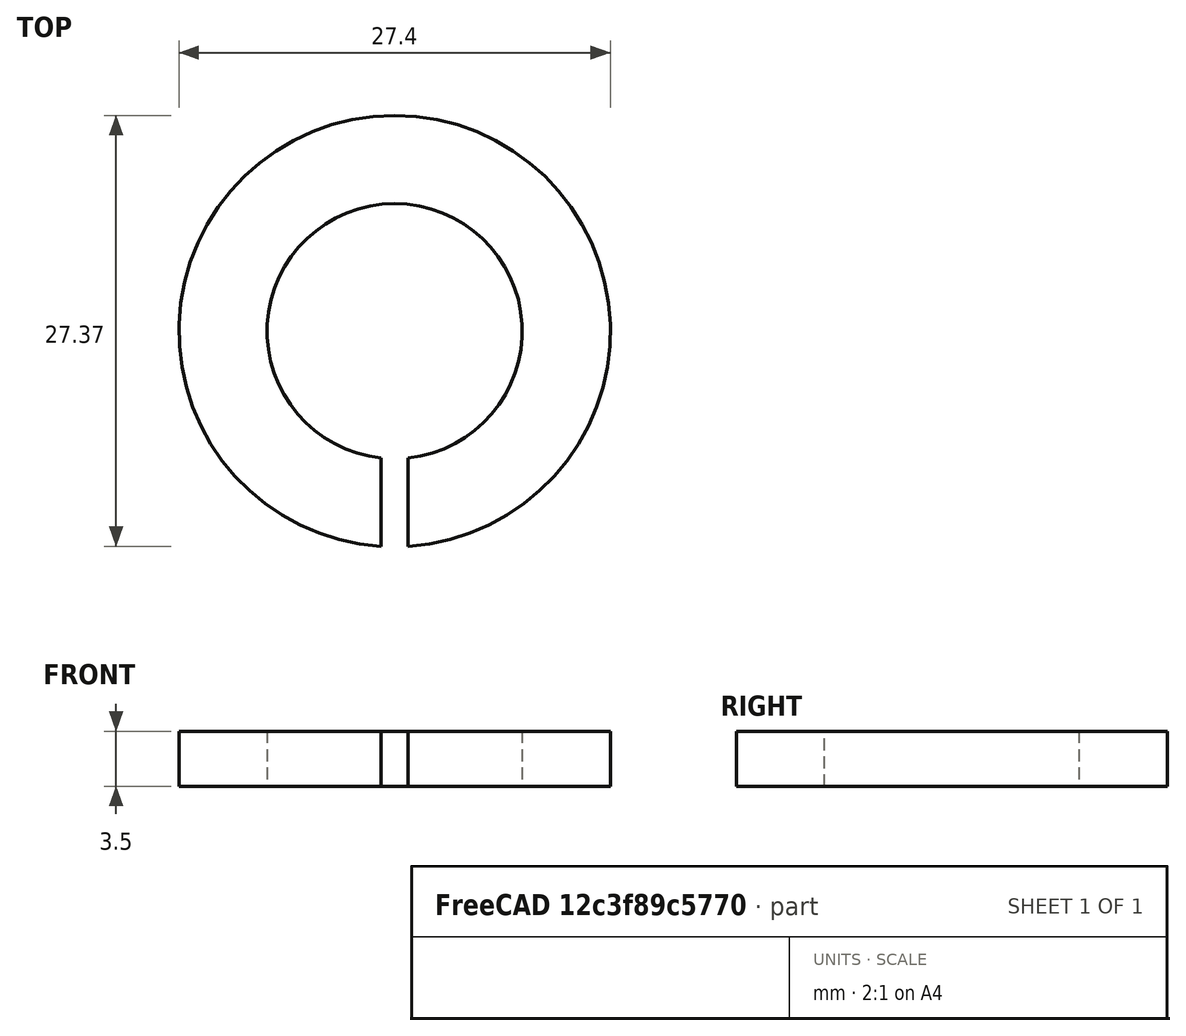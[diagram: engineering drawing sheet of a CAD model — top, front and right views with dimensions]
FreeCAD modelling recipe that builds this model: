
FCSTD DOCUMENT  (FreeCAD 0.15R4651 (Git))
Label: Federring_DIN127-B16
License: All rights reserved
LicenseURL: http://de.wikipedia.org/wiki/Alle_Rechte_vorbehalten
objects: Sketcher::SketchObject×1, PartDesign::Pad×1
note: 3 computed .brp shape members not serialized (recipe doc carries the construction recipe); baked Part::Feature solids carry a one-line shape summary decoded from their .brp

FEATURE [Sketcher::SketchObject] Sketch
  sketch-geometry (4):
    g0: ArcOfCircle CenterX=0 CenterY=0 CenterZ=0 NormalX=0 NormalY=0 NormalZ=1 Radius=8.1 StartAngle=4.81752 EndAngle=10.8904
    g1: ArcOfCircle CenterX=0 CenterY=0 CenterZ=0 NormalX=0 NormalY=0 NormalZ=1 Radius=13.7 StartAngle=4.77447 EndAngle=10.9335
    g2: LineSegment StartX=0.85 StartY=-8.05528 StartZ=0 EndX=0.85 EndY=-13.6736 EndZ=0
    g3: LineSegment StartX=-0.85 StartY=-13.6736 StartZ=0 EndX=-0.85 EndY=-8.05528 EndZ=0
  constraints (12):
    c: Coincident(g0,g-1)
    c: Coincident(g1,g-1)
    c: Vertical(g2)
    c: Vertical(g3)
    c: Coincident(g0,g2)
    c: Coincident(g0,g3)
    c: Coincident(g1,g2)
    c: Coincident(g1,g3)
    c: Symmetric(g1,g1,g-2)
    c: Radius(g0) = 8.1
    c: Radius(g1) = 13.7
    c: DistanceX(g1,g1) = -1.7
FEATURE [PartDesign::Pad] Pad  label="Federring DIN 127-B 16 #"
  Length = 3.5
  Length2 = 100
  Midplane = true
  Sketch = -> Sketch
  Type = 0
